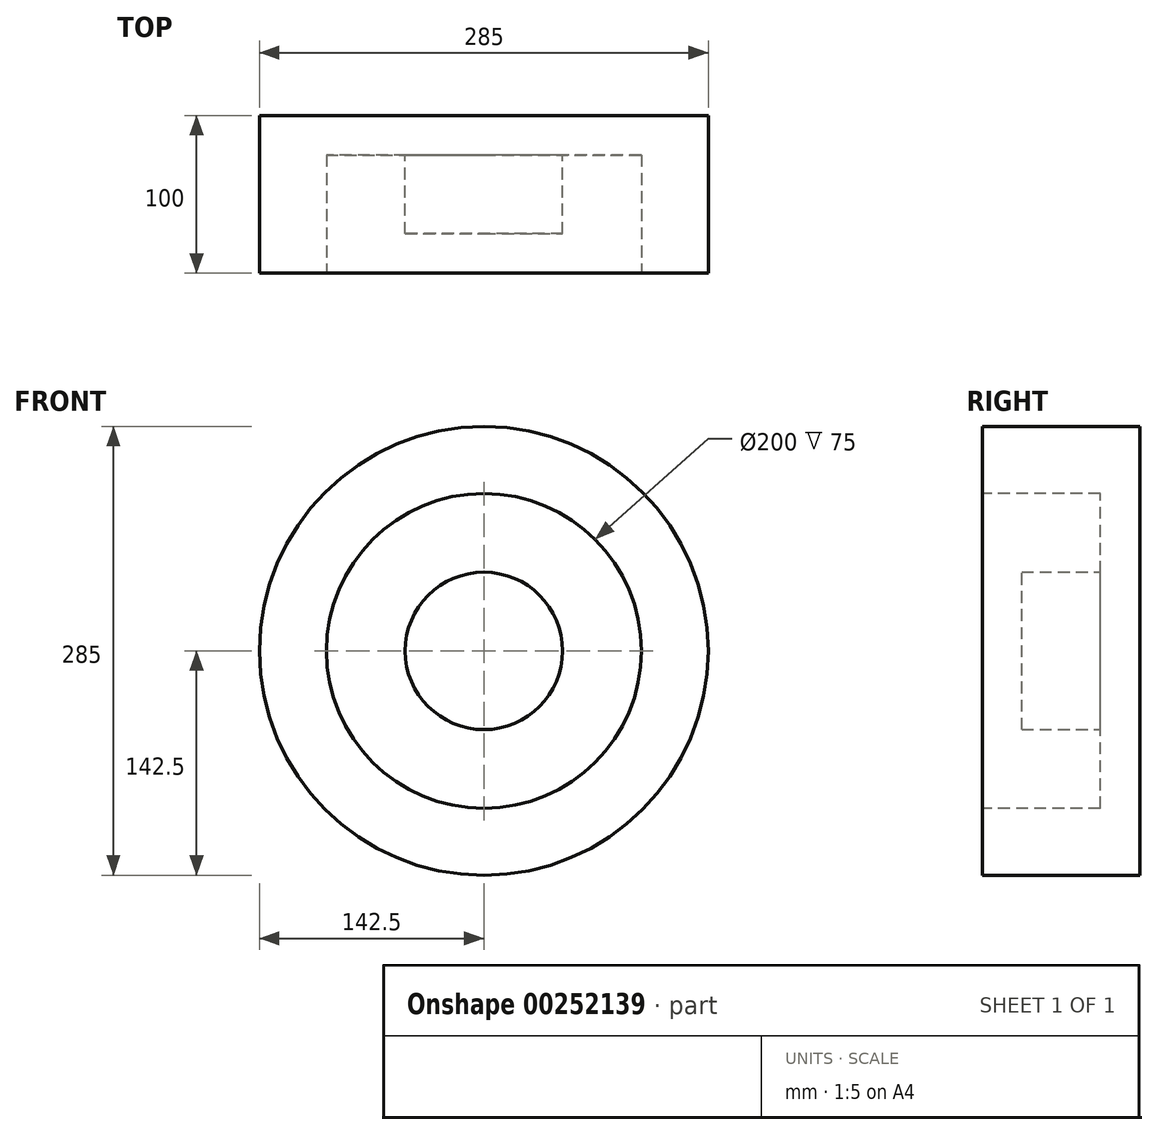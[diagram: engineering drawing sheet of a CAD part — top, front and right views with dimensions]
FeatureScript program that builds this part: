
annotation { "Feature Type Name" : "Feature", "Feature Type Description" : "" }
export const myFeature = defineFeature(function(context is Context, id is Id, definition is map)
    precondition{}
    {
        {
            var Q0;
            Q0=qCreatedBy(makeId("Front.planeOp"),FACE);
            var sketch = newSketch(context, id + "F0", { "sketchPlane" : qUnion([Q0])});
            skCircle(sketch, "E0", {"center": v(0, 0) * mm, "radius": 142.5 * mm});
            skSolve(sketch);
        }
        {
            var Q0;
            Q0=makeQuery(id+"F0.imprint","IMPRINT",FACE,{"disambiguationData":[TD([[makeQuery(id+"F0.imprint","IMPRINT",EDGE,{"derivedFrom":sQuery(id+"F0.wireOp",EDGE,"E0")}),1.0]])]});
            extrude(context, id + "F1", {"entities" : qUnion([Q0]), "depth" : 100 * mm});
        }
        {
            var Q0;
            Q0=makeQuery(id+"F1.opExtrude","CAP_FACE",FACE,{"disambiguationData":[OSD([sQuery(id+"F0.wireOp",EDGE,"E0")])],"isStart":false});
            var sketch = newSketch(context, id + "F2", { "sketchPlane" : qUnion([Q0])});
            skCircle(sketch, "E1", {"center": v(0, 0) * mm, "radius": 100 * mm});
            skSolve(sketch);
        }
        {
            var Q0;
            Q0=makeQuery(id+"F2.imprint","IMPRINT",FACE,{"disambiguationData":[TD([[makeQuery(id+"F2.imprint","IMPRINT",EDGE,{"derivedFrom":sQuery(id+"F2.wireOp",EDGE,"E1")}),1.0]])]});
            extrude(context, id + "F3", {"entities" : qUnion([Q0]), "operationType" : NewBodyOperationType.REMOVE, "oppositeDirection" : true, "depth" : 75 * mm});
        }
        {
            var Q0;
            Q0=makeQuery(id+"F3.boolean.opBoolean","COPY",FACE,{"derivedFrom":makeQuery(id+"F3.opExtrude","CAP_FACE",FACE,{"disambiguationData":[OSD([sQuery(id+"F2.wireOp",EDGE,"E1")])],"isStart":false})});
            var sketch = newSketch(context, id + "F4", { "sketchPlane" : qUnion([Q0])});
            skCircle(sketch, "E2", {"center": v(0, 0) * mm, "radius": 50 * mm});
            skSolve(sketch);
        }
        {
            var Q0;
            Q0=makeQuery(id+"F4.imprint","IMPRINT",FACE,{"disambiguationData":[TD([[makeQuery(id+"F4.imprint","IMPRINT",EDGE,{"derivedFrom":sQuery(id+"F4.wireOp",EDGE,"E2")}),1.0]])]});
            extrude(context, id + "F5", {"entities" : qUnion([Q0]), "operationType" : NewBodyOperationType.ADD, "depth" : 50 * mm});
        }
    });
